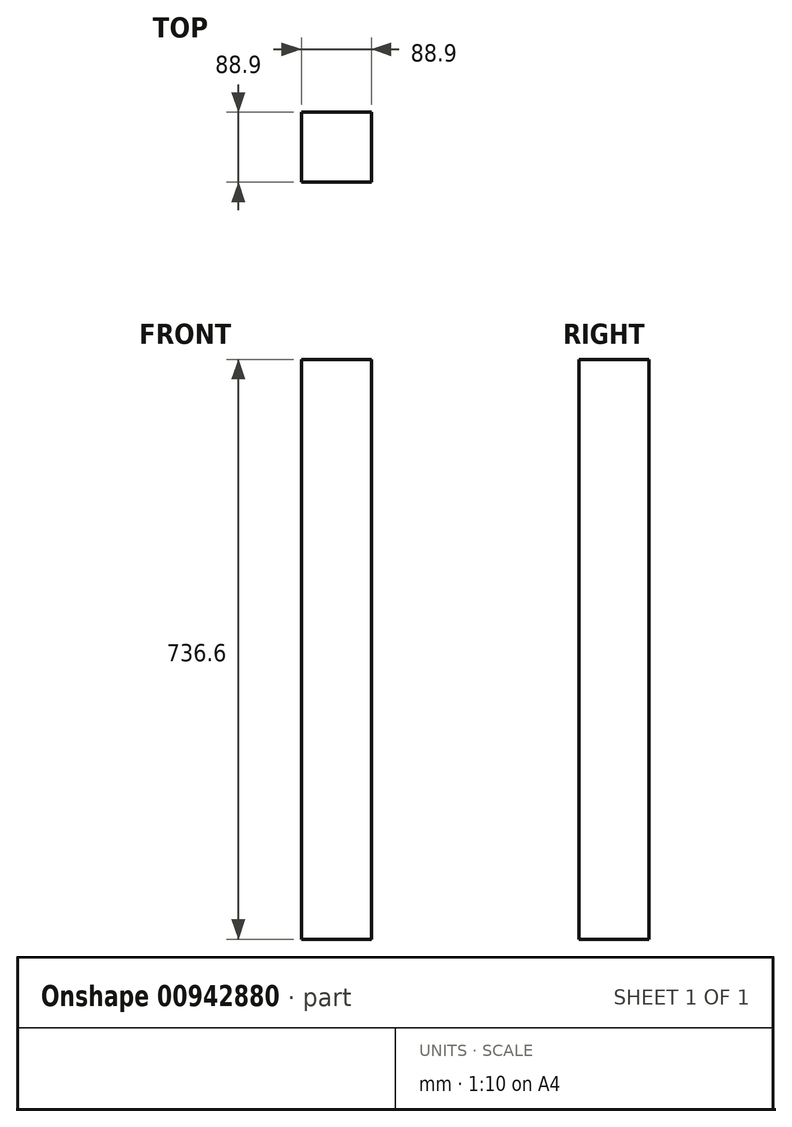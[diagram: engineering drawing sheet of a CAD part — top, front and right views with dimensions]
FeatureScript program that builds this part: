
annotation { "Feature Type Name" : "Feature", "Feature Type Description" : "" }
export const myFeature = defineFeature(function(context is Context, id is Id, definition is map)
    precondition{}
    {
        {
            var Q0;
            Q0=qCreatedBy(makeId("Front.planeOp"),FACE);
            var sketch = newSketch(context, id + "F0", { "sketchPlane" : qUnion([Q0])});
            skLineSegment(sketch, "E0.bottom", {"start": v(0, 0) * mm, "end": v(88.9, 0) * mm});
            skLineSegment(sketch, "E0.top", {"start": v(0, -736.6) * mm, "end": v(88.9, -736.6) * mm});
            skLineSegment(sketch, "E0.left", {"start": v(0, 0) * mm, "end": v(0, -736.6) * mm});
            skLineSegment(sketch, "E0.right", {"start": v(88.9, 0) * mm, "end": v(88.9, -736.6) * mm});
            skSolve(sketch);
        }
        {
            var Q0;
            Q0=qSketchRegion(id+"F0",true);
            extrude(context, id + "F1", {"entities" : qUnion([Q0]), "depth" : 88.9 * mm, "offsetDistance" : 25.4 * mm});
        }
    });
